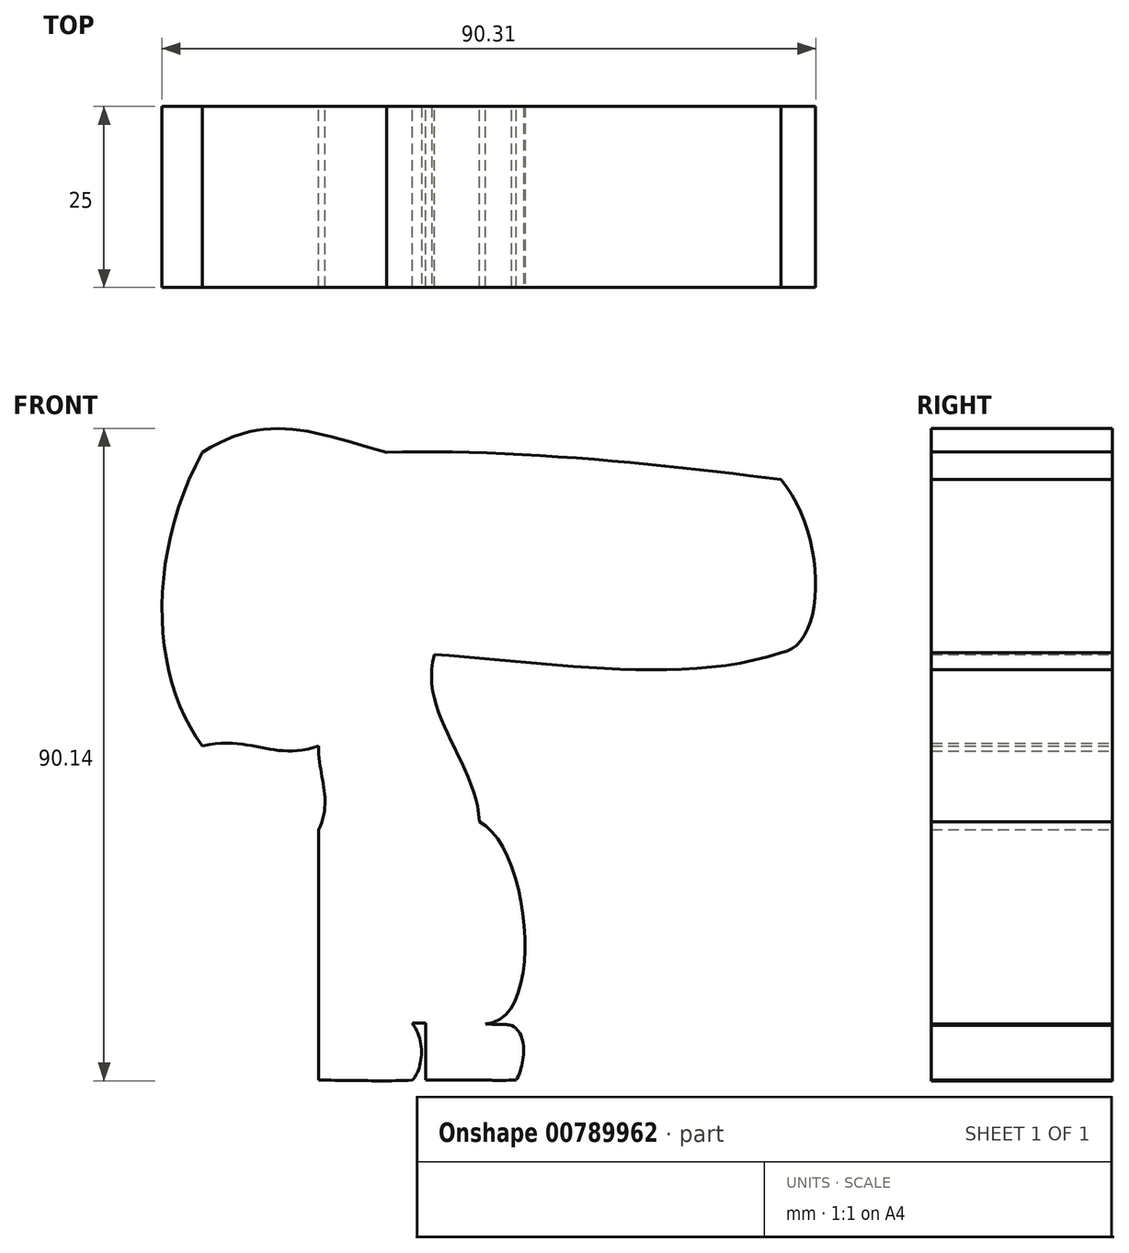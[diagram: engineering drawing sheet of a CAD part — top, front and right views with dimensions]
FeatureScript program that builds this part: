
annotation { "Feature Type Name" : "Feature", "Feature Type Description" : "" }
export const myFeature = defineFeature(function(context is Context, id is Id, definition is map)
    precondition{}
    {
        {
            var Q0;
            Q0=qCreatedBy(makeId("Front.planeOp"),FACE);
            var sketch = newSketch(context, id + "F0", { "sketchPlane" : qUnion([Q0])});
            skFitSpline(sketch, "E0", {"points": [v(0, 27.69) * mm, v(54.48, 23.92) * mm], "startDerivative": vector(50.04, 1.55) * mm, "endDerivative": vector(48.28, -6.52) * mm});
            skFitSpline(sketch, "E1", {"points": [v(54.48, 23.92) * mm, v(54.48, 0) * mm], "startDerivative": vector(19.23, -22.2) * mm, "endDerivative": vector(-19.32, -2.68) * mm});
            skFitSpline(sketch, "E2", {"points": [v(0, 0) * mm, v(54.48, 0) * mm], "startDerivative": vector(49.56, -0.11) * mm, "endDerivative": vector(47.32, 15.93) * mm});
            skFitSpline(sketch, "E3", {"points": [v(0, 27.69) * mm, v(-25.41, 27.69) * mm], "startDerivative": vector(-32.63, 9.33) * mm, "endDerivative": vector(-26.56, -16.6) * mm});
            skFitSpline(sketch, "E4", {"points": [v(-25.41, -12.86) * mm, v(-9.39, -12.86) * mm], "startDerivative": vector(21.25, 4.35) * mm, "endDerivative": vector(18.5, 6.58) * mm});
            skFitSpline(sketch, "E5", {"points": [v(-9.39, -12.86) * mm, v(-9.39, -24.43) * mm], "startDerivative": vector(0, -13.49) * mm, "endDerivative": vector(-6.09, -12.1) * mm});
            skFitSpline(sketch, "E6", {"points": [v(0, -12.86) * mm, v(0, -24.43) * mm], "startDerivative": vector(0, -13.49) * mm, "endDerivative": vector(0, -13.49) * mm});
            skFitSpline(sketch, "E7", {"points": [v(0, 0) * mm, v(0, -12.86) * mm], "startDerivative": vector(0, -11) * mm, "endDerivative": vector(0, -11) * mm});
            skFitSpline(sketch, "E8", {"points": [v(6.64, -0.24) * mm, v(12.86, -23.33) * mm], "startDerivative": vector(-6.95, -23.71) * mm, "endDerivative": vector(1.6, -24.65) * mm});
            skFitSpline(sketch, "E9", {"points": [v(-9.39, -24.43) * mm, v(-9.39, -49.1) * mm], "startDerivative": vector(0, -24.6) * mm, "endDerivative": vector(0, -24.6) * mm});
            skFitSpline(sketch, "E10", {"points": [v(12.86, -23.33) * mm, v(12.86, -51.3) * mm], "startDerivative": vector(21.75, -11.6) * mm, "endDerivative": vector(-28.22, 3.05) * mm});
            skFitSpline(sketch, "E11", {"points": [v(17.93, -59.07) * mm, v(12.86, -59.07) * mm], "startDerivative": vector(-13.64, -0.16) * mm, "endDerivative": vector(-13.4, 0.07) * mm});
            skFitSpline(sketch, "E12", {"points": [v(-9.39, -49.1) * mm, v(-9.39, -59.07) * mm], "startDerivative": vector(0, -10.12) * mm, "endDerivative": vector(0, -10.12) * mm});
            skFitSpline(sketch, "E13", {"points": [v(-9.39, -59.07) * mm, v(3.57, -59.07) * mm], "startDerivative": vector(13.49, 0) * mm, "endDerivative": vector(13.18, 0.58) * mm});
            skFitSpline(sketch, "E14", {"points": [v(3.57, -51.2) * mm, v(3.57, -59.07) * mm], "startDerivative": vector(5.42, -7.16) * mm, "endDerivative": vector(-4.72, -5.09) * mm});
            skFitSpline(sketch, "E15", {"points": [v(3.57, -51.2) * mm, v(0, -51.2) * mm], "startDerivative": vector(-2.68, 0) * mm, "endDerivative": vector(-2.68, -1.64) * mm});
            skFitSpline(sketch, "E16", {"points": [v(0, -51.2) * mm, v(0, -45.78) * mm, v(0, -45.6) * mm], "startDerivative": vector(0, 8.73) * mm, "endDerivative": vector(0, 0.73) * mm});
            skFitSpline(sketch, "E17", {"points": [v(12.86, -59.07) * mm, v(5.41, -59.07) * mm], "startDerivative": vector(-3.17, 0) * mm, "endDerivative": vector(-3.17, 0) * mm});
            skFitSpline(sketch, "E18", {"points": [v(5.41, -59.07) * mm, v(5.41, -51.2) * mm], "startDerivative": vector(0, 7.93) * mm, "endDerivative": vector(0, 7.93) * mm});
            skFitSpline(sketch, "E19", {"points": [v(-25.41, 27.69) * mm, v(-25.41, -12.86) * mm], "startDerivative": vector(-23.38, -42.66) * mm, "endDerivative": vector(21.4, -27.7) * mm});
            skFitSpline(sketch, "E20", {"points": [v(3.57, -51.2) * mm, v(5.41, -51.2) * mm], "startDerivative": vector(1.84, 0) * mm, "endDerivative": vector(1.84, 0) * mm});
            skFitSpline(sketch, "E21", {"points": [v(12.86, -51.3) * mm, v(17.28, -51.5) * mm], "startDerivative": vector(15.36, -0.47) * mm, "endDerivative": vector(4.1, -0.52) * mm});
            skFitSpline(sketch, "E22", {"points": [v(17.28, -51.5) * mm, v(17.93, -59.07) * mm], "startDerivative": vector(7.29, -3.57) * mm, "endDerivative": vector(-3.47, -6.35) * mm});
            skSolve(sketch);
        }
        {
            var Q0;
            Q0 = qSketchRegion(id + "F0", true);
            extrude(context, id + "F1", {"entities" : qUnion([Q0]), "depth" : 25 * mm, "offsetDistance" : 25 * mm});
        }
        {
            var Q0;
            Q0 = qSketchRegion(id + "F0", true);
            extrude(context, id + "F2", {"entities" : qUnion([Q0]), "operationType" : NewBodyOperationType.ADD, "depth" : 25 * mm, "offsetDistance" : 25 * mm});
        }
    });
